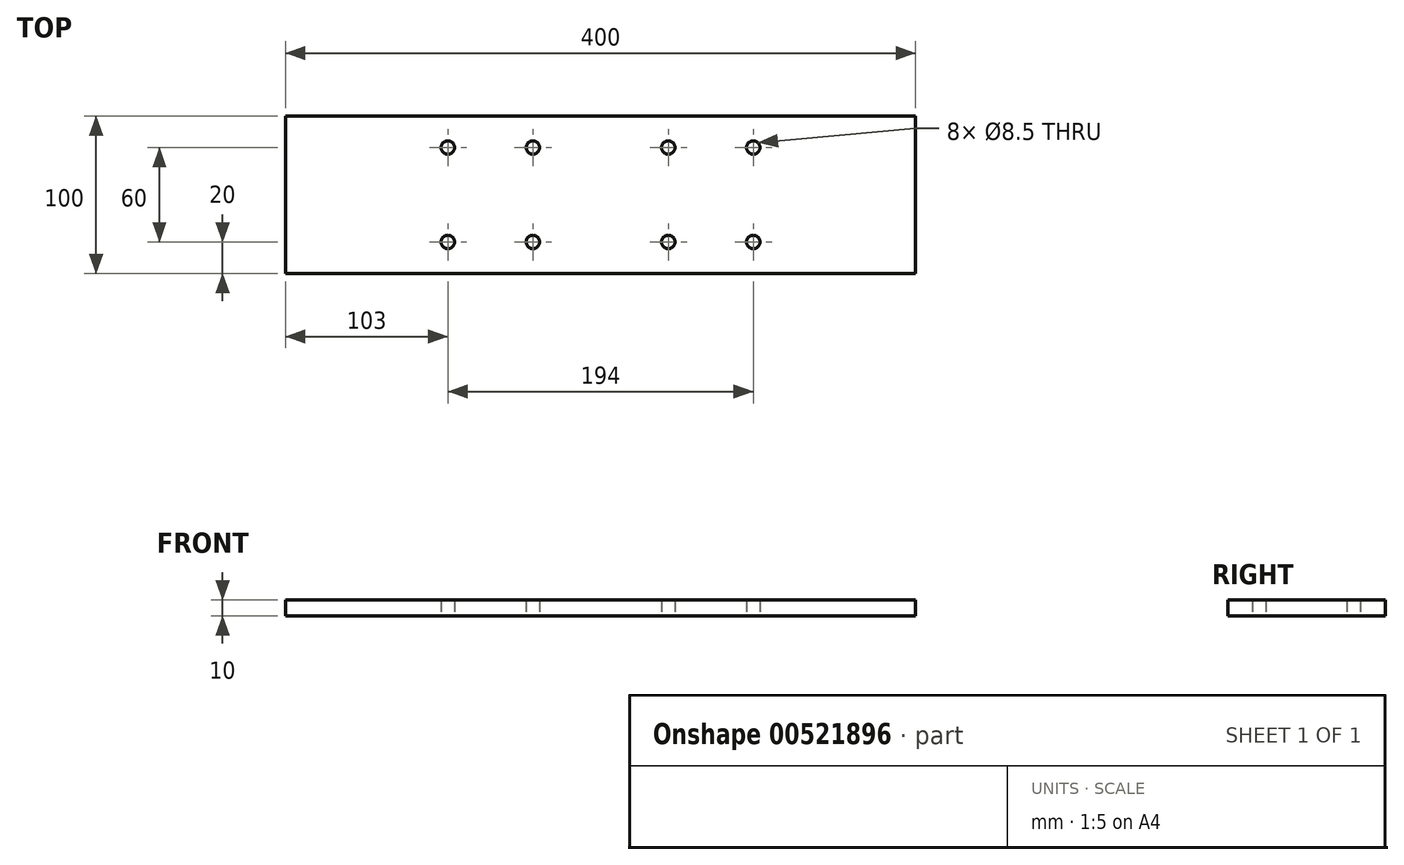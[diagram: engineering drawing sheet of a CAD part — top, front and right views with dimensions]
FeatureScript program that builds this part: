
annotation { "Feature Type Name" : "Feature", "Feature Type Description" : "" }
export const myFeature = defineFeature(function(context is Context, id is Id, definition is map)
    precondition{}
    {
        {
            var Q0;
            Q0=qCreatedBy(makeId("Top.planeOp"),FACE);
            var sketch = newSketch(context, id + "F0", { "sketchPlane" : qUnion([Q0])});
            skLineSegment(sketch, "E0.bottom", {"start": v(-103, -80) * mm, "end": v(297, -80) * mm});
            skLineSegment(sketch, "E0.top", {"start": v(-103, 20) * mm, "end": v(297, 20) * mm});
            skLineSegment(sketch, "E0.left", {"start": v(-103, -80) * mm, "end": v(-103, 20) * mm});
            skLineSegment(sketch, "E0.right", {"start": v(297, -80) * mm, "end": v(297, 20) * mm});
            skCircle(sketch, "E1", {"center": v(0, 0) * mm, "radius": 4.25 * mm});
            skCircle(sketch, "E2", {"center": v(54, 0) * mm, "radius": 4.25 * mm});
            skCircle(sketch, "E3", {"center": v(0, -60) * mm, "radius": 4.25 * mm});
            skCircle(sketch, "E4", {"center": v(54, -60) * mm, "radius": 4.25 * mm});
            skLineSegment(sketch, "E5", {"start": v(-103, -30) * mm, "end": v(297, -30) * mm, "construction": true});
            skLineSegment(sketch, "E6", {"start": v(97, -80) * mm, "end": v(97, 20) * mm, "construction": true});
            skCircle(sketch, "E7", {"center": v(140, 0) * mm, "radius": 4.25 * mm});
            skCircle(sketch, "E8", {"center": v(194, 0) * mm, "radius": 4.25 * mm});
            skCircle(sketch, "E9", {"center": v(194, -60) * mm, "radius": 4.25 * mm});
            skCircle(sketch, "E10", {"center": v(140, -60) * mm, "radius": 4.25 * mm});
            skSolve(sketch);
        }
        {
            var Q0;
            Q0 = qSketchRegion(id + "F0", true);
            extrude(context, id + "F1", {"entities" : qUnion([Q0]), "depth" : 10 * mm, "offsetDistance" : 25 * mm});
        }
    });
